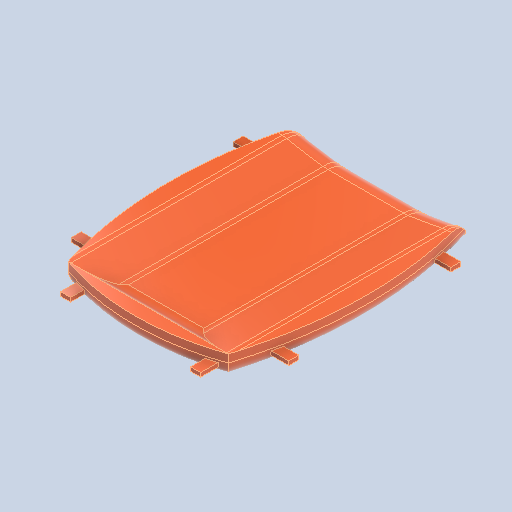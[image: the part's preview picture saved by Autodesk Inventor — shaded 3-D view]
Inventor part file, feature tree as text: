
AUTODESK INVENTOR PART (.ipt)
format: ipt  version: 2023 (Build 270158000, 158)  size: 363,008 bytes
history: native  units: in
note: dims shown in document units (in); Inventor stores cm internally (conversion verified against a paired STEP export)
features: extrude x4, fillet x3, sketch x3, plane x1
ambient origin geometry x8: Origin, YZ Plane, XZ Plane, XY Plane, X Axis, Y Axis, Z Axis, Center Point
bodies: Solid1 (feature_tree)
feature tree (11):
  extrude  "Extrusion1"  Depth=2.3622in
  extrude  "Extrusion2"  Depth=23.622in
  fillet  "Fillet2"  Radius=7.874in
  fillet  "Fillet3"  Radius=1.5748in
  fillet  "Fillet4"  Radius=23.622in
  plane  "Work Plane1"
  sketch  "Sketch3"  dims[d9=39.3701in d10=39.3701in d11=23.622in d12=7.874in d13=7.874in d14=2.3622in d15=0.0in d17=2.3622in d18=2.3622in d19=1.5748in d20=-1.1811in d23=15.2893in d26=1.9685in d27=0.9843in d28=2.9528in d32=1.9685in d33=2.9528in d34=0.9843in d35=1.9685in d39=2.3622in d40=0.9843in d41=2.3622in d43=2.3622in d44=3.3465in d45=0.9843in d46=2.3622in d47=0.3937in d48=0.0in d49=2.8255in d50=2.8255in d51=2.8255in d52=0.3937in d53=0.0in d54=2.8255in d16=0.0197in d21=0.0in d22=0.0in]
  extrude  "Extrusion3"  Depth=0.3937in
  extrude  "Extrusion4"  Depth=23.622in
  sketch  "Sketch1"  dims[d0=2.3622in d1=2.3622in]
  sketch  "Sketch2"  dims[d2=15.748in d3=3.937in d5=7.874in d6=1.5748in d7=23.622in d8=0.0in]
